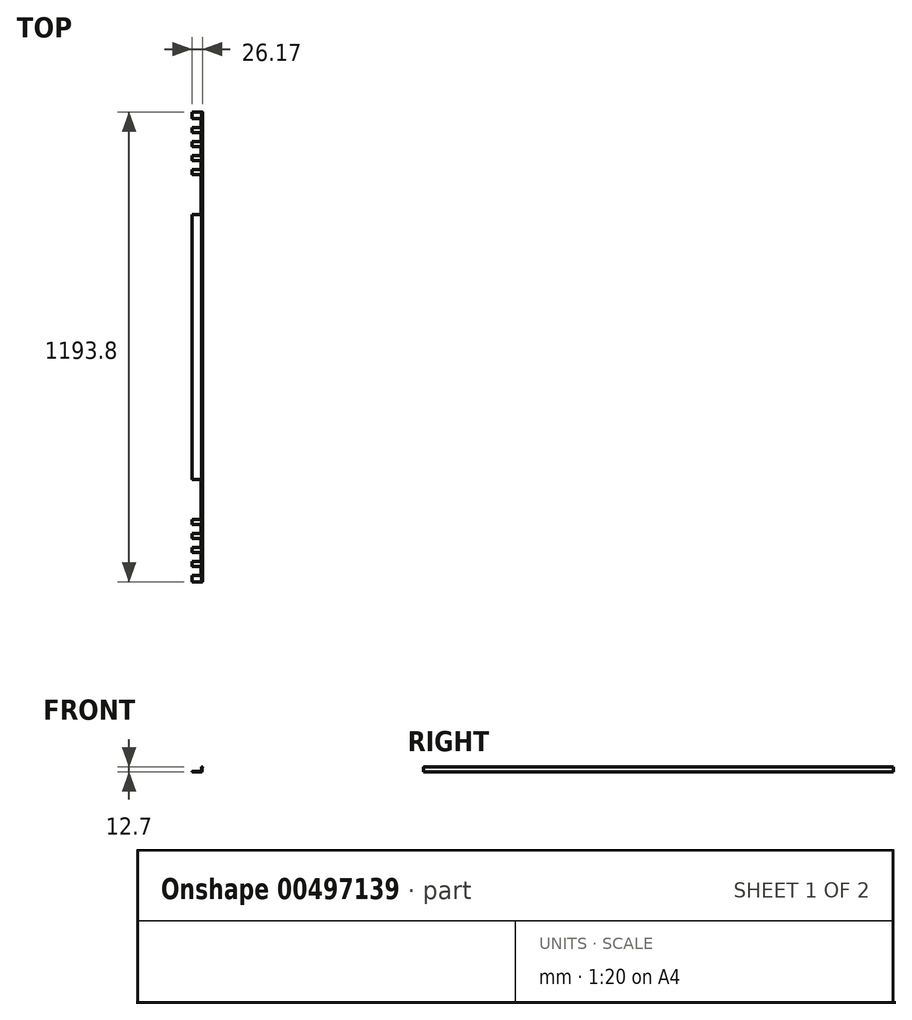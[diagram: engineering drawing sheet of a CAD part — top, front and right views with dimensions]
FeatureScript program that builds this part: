
annotation { "Feature Type Name" : "Feature", "Feature Type Description" : "" }
export const myFeature = defineFeature(function(context is Context, id is Id, definition is map)
    precondition{}
    {
        {
            var Q0;
            Q0=qCreatedBy(makeId("Front.planeOp"),FACE);
            var sketch = newSketch(context, id + "F0", { "sketchPlane" : qUnion([Q0])});
            skLineSegment(sketch, "E0", {"start": v(1.52, 9.1) * mm, "end": v(1.52, 0.76) * mm});
            skLineSegment(sketch, "E1", {"start": v(-0.76, -1.52) * mm, "end": v(-23.88, -1.52) * mm});
            skLineSegment(sketch, "E2", {"start": v(-23.88, -1.52) * mm, "end": v(-23.88, 0) * mm});
            skLineSegment(sketch, "E3", {"start": v(-23.88, 0) * mm, "end": v(-0.76, 0) * mm});
            skLineSegment(sketch, "E4", {"start": v(0, 0.76) * mm, "end": v(0, 9.65) * mm});
            skLineSegment(sketch, "E5", {"start": v(1.52, 11.18) * mm, "end": v(1.52, 11.18) * mm});
            skPoint(sketch, "E6.visualSharp", {"position": v(0, 0) * mm});
            skArc(sketch, "E6.filletArc", {"start": v(-0.76, 0) * mm, "mid": v(-0.22, 0.22) * mm, "end": v(0, 0.76) * mm});
            skPoint(sketch, "E7.visualSharp", {"position": v(1.52, -1.52) * mm});
            skArc(sketch, "E7.filletArc", {"start": v(-0.76, -1.52) * mm, "mid": v(0.85, -0.85) * mm, "end": v(1.52, 0.76) * mm});
            skArc(sketch, "E8", {"start": v(1.9, 9.75) * mm, "mid": v(2.26, 10.61) * mm, "end": v(1.52, 11.18) * mm});
            skPoint(sketch, "E9.visualSharp", {"position": v(0, 11.18) * mm});
            skArc(sketch, "E9.filletArc", {"start": v(1.52, 11.18) * mm, "mid": v(0.45, 10.73) * mm, "end": v(0, 9.65) * mm});
            skArc(sketch, "E10.filletArc", {"start": v(1.9, 9.75) * mm, "mid": v(1.63, 9.48) * mm, "end": v(1.52, 9.1) * mm});
            skSolve(sketch);
        }
        {
            var Q0;
            Q0 = qSketchRegion(id + "F0", true);
            extrude(context, id + "F1", {"entities" : qUnion([Q0]), "depth" : 596.9 * mm});
        }
        {
            var Q0;
            Q0=makeQuery(id+"F1.opExtrude","SWEPT_EDGE",EDGE,{"disambiguationData":[OSD([sQuery(id+"F0.wireOp",EDGE,"E2"),sQuery(id+"F0.wireOp",EDGE,"E3")])]});
            var Q1;
            Q1=makeQuery(id+"F1.opExtrude","SWEPT_EDGE",EDGE,{"disambiguationData":[OSD([sQuery(id+"F0.wireOp",EDGE,"E1"),sQuery(id+"F0.wireOp",EDGE,"E2")])]});
            fillet(context, id + "F2", {"entities" : qUnion([Q0, Q1]), "radius" : 0.76 * mm, "tangentPropagation" : true, "allowEdgeOverflow" : false});
        }
        {
            var Q0;
            Q0=qCreatedBy(makeId("Top.planeOp"),FACE);
            var sketch = newSketch(context, id + "F3", { "sketchPlane" : qUnion([Q0])});
            skLineSegment(sketch, "E11.bottom", {"start": v(-52.32, -336.55) * mm, "end": v(-1.52, -336.55) * mm});
            skLineSegment(sketch, "E11.top", {"start": v(-52.32, -438.15) * mm, "end": v(-1.52, -438.15) * mm});
            skLineSegment(sketch, "E11.left", {"start": v(-52.32, -336.55) * mm, "end": v(-52.32, -438.15) * mm});
            skLineSegment(sketch, "E11.right", {"start": v(-1.52, -336.55) * mm, "end": v(-1.52, -438.15) * mm});
            skSolve(sketch);
        }
        {
            var Q0;
            Q0 = qSketchRegion(id + "F3", true);
            extrude(context, id + "F4", {"entities" : qUnion([Q0]), "operationType" : NewBodyOperationType.REMOVE, "endBound" : BoundingType.THROUGH_ALL, "oppositeDirection" : true, "depth" : 25.4 * mm});
        }
        {
            var Q0;
            Q0=qCreatedBy(makeId("Top.planeOp"),FACE);
            var sketch = newSketch(context, id + "F5", { "sketchPlane" : qUnion([Q0])});
            skLineSegment(sketch, "E12.bottom", {"start": v(-52.32, -450.85) * mm, "end": v(-1.52, -450.85) * mm});
            skLineSegment(sketch, "E12.top", {"start": v(-52.32, -473.71) * mm, "end": v(-1.52, -473.71) * mm});
            skLineSegment(sketch, "E12.left", {"start": v(-52.32, -450.85) * mm, "end": v(-52.32, -473.71) * mm});
            skLineSegment(sketch, "E12.right", {"start": v(-1.52, -450.85) * mm, "end": v(-1.52, -473.71) * mm});
            skLineSegment(sketch, "E13.bottom", {"start": v(-52.32, -486.41) * mm, "end": v(-1.52, -486.41) * mm});
            skLineSegment(sketch, "E13.top", {"start": v(-52.32, -509.27) * mm, "end": v(-1.52, -509.27) * mm});
            skLineSegment(sketch, "E13.left", {"start": v(-52.32, -486.41) * mm, "end": v(-52.32, -509.27) * mm});
            skLineSegment(sketch, "E13.right", {"start": v(-1.52, -486.41) * mm, "end": v(-1.52, -509.27) * mm});
            skLineSegment(sketch, "E14.bottom", {"start": v(-52.32, -521.97) * mm, "end": v(-1.52, -521.97) * mm});
            skLineSegment(sketch, "E14.top", {"start": v(-52.32, -544.83) * mm, "end": v(-1.52, -544.83) * mm});
            skLineSegment(sketch, "E14.left", {"start": v(-52.32, -521.97) * mm, "end": v(-52.32, -544.83) * mm});
            skLineSegment(sketch, "E14.right", {"start": v(-1.52, -521.97) * mm, "end": v(-1.52, -544.83) * mm});
            skLineSegment(sketch, "E15.bottom", {"start": v(-52.32, -557.53) * mm, "end": v(-1.52, -557.53) * mm});
            skLineSegment(sketch, "E15.top", {"start": v(-52.32, -580.4) * mm, "end": v(-1.52, -580.4) * mm});
            skLineSegment(sketch, "E15.left", {"start": v(-52.32, -557.53) * mm, "end": v(-52.32, -580.4) * mm});
            skLineSegment(sketch, "E15.right", {"start": v(-1.52, -557.53) * mm, "end": v(-1.52, -580.4) * mm});
            skSolve(sketch);
        }
        {
            var Q0;
            Q0 = qSketchRegion(id + "F5", true);
            extrude(context, id + "F6", {"entities" : qUnion([Q0]), "operationType" : NewBodyOperationType.REMOVE, "endBound" : BoundingType.THROUGH_ALL, "oppositeDirection" : true, "depth" : 25.4 * mm});
        }
        {
            var Q0;
            Q0=makeQuery(id+"F4.boolean.opBoolean","COPY",EDGE,{"derivedFrom":makeQuery(id+"F4.opExtrude","SWEPT_EDGE",EDGE,{"disambiguationData":[OSD([sQuery(id+"F3.wireOp",EDGE,"E11.bottom"),sQuery(id+"F3.wireOp",EDGE,"E11.right")])]})});
            var Q1;
            Q1=makeQuery(id+"F4.boolean.opBoolean","COPY",EDGE,{"derivedFrom":makeQuery(id+"F4.opExtrude","SWEPT_EDGE",EDGE,{"disambiguationData":[OSD([sQuery(id+"F3.wireOp",EDGE,"E11.top"),sQuery(id+"F3.wireOp",EDGE,"E11.right")])]})});
            var Q2;
            Q2=makeQuery(id+"F6.boolean.opBoolean","COPY",EDGE,{"derivedFrom":makeQuery(id+"F6.opExtrude","SWEPT_EDGE",EDGE,{"disambiguationData":[OSD([sQuery(id+"F5.wireOp",EDGE,"E12.bottom"),sQuery(id+"F5.wireOp",EDGE,"E12.right")])]})});
            var Q3;
            Q3=makeQuery(id+"F6.boolean.opBoolean","COPY",EDGE,{"derivedFrom":makeQuery(id+"F6.opExtrude","SWEPT_EDGE",EDGE,{"disambiguationData":[OSD([sQuery(id+"F5.wireOp",EDGE,"E12.top"),sQuery(id+"F5.wireOp",EDGE,"E12.right")])]})});
            var Q4;
            Q4=makeQuery(id+"F6.boolean.opBoolean","COPY",EDGE,{"derivedFrom":makeQuery(id+"F6.opExtrude","SWEPT_EDGE",EDGE,{"disambiguationData":[OSD([sQuery(id+"F5.wireOp",EDGE,"E13.top"),sQuery(id+"F5.wireOp",EDGE,"E13.right")])]})});
            var Q5;
            Q5=makeQuery(id+"F6.boolean.opBoolean","COPY",EDGE,{"derivedFrom":makeQuery(id+"F6.opExtrude","SWEPT_EDGE",EDGE,{"disambiguationData":[OSD([sQuery(id+"F5.wireOp",EDGE,"E14.top"),sQuery(id+"F5.wireOp",EDGE,"E14.right")])]})});
            var Q6;
            Q6=makeQuery(id+"F6.boolean.opBoolean","COPY",EDGE,{"derivedFrom":makeQuery(id+"F6.opExtrude","SWEPT_EDGE",EDGE,{"disambiguationData":[OSD([sQuery(id+"F5.wireOp",EDGE,"E15.top"),sQuery(id+"F5.wireOp",EDGE,"E15.right")])]})});
            var Q7;
            Q7=makeQuery(id+"F6.boolean.opBoolean","COPY",EDGE,{"derivedFrom":makeQuery(id+"F6.opExtrude","SWEPT_EDGE",EDGE,{"disambiguationData":[OSD([sQuery(id+"F5.wireOp",EDGE,"E13.bottom"),sQuery(id+"F5.wireOp",EDGE,"E13.right")])]})});
            var Q8;
            Q8=makeQuery(id+"F6.boolean.opBoolean","COPY",EDGE,{"derivedFrom":makeQuery(id+"F6.opExtrude","SWEPT_EDGE",EDGE,{"disambiguationData":[OSD([sQuery(id+"F5.wireOp",EDGE,"E14.bottom"),sQuery(id+"F5.wireOp",EDGE,"E14.right")])]})});
            var Q9;
            Q9=makeQuery(id+"F6.boolean.opBoolean","COPY",EDGE,{"derivedFrom":makeQuery(id+"F6.opExtrude","SWEPT_EDGE",EDGE,{"disambiguationData":[OSD([sQuery(id+"F5.wireOp",EDGE,"E15.bottom"),sQuery(id+"F5.wireOp",EDGE,"E15.right")])]})});
            fillet(context, id + "F7", {"entities" : qUnion([Q0, Q1, Q2, Q3, Q4, Q5, Q6, Q7, Q8, Q9]), "radius" : 3.17 * mm, "tangentPropagation" : true, "allowEdgeOverflow" : false});
        }
        {
            var Q0;
            Q0=makeQuery(id+"F1.opExtrude","SWEPT_BODY",BODY,{"disambiguationData":[OSD([sQuery(id+"F0.wireOp",EDGE,"E0"),sQuery(id+"F0.wireOp",EDGE,"E1"),sQuery(id+"F0.wireOp",EDGE,"E2"),sQuery(id+"F0.wireOp",EDGE,"E3"),sQuery(id+"F0.wireOp",EDGE,"E4"),sQuery(id+"F0.wireOp",EDGE,"E6.filletArc"),sQuery(id+"F0.wireOp",EDGE,"E7.filletArc"),sQuery(id+"F0.wireOp",EDGE,"E8"),sQuery(id+"F0.wireOp",EDGE,"E9.filletArc"),sQuery(id+"F0.wireOp",EDGE,"E10.filletArc")])]});
            var Q1;
            Q1=qCreatedBy(makeId("Front.planeOp"),FACE);
            mirror(context, id + "F8", {"operationType" : NewBodyOperationType.ADD, "entities" : qUnion([Q0]), "mirrorPlane" : qUnion([Q1])});
        }
    });
